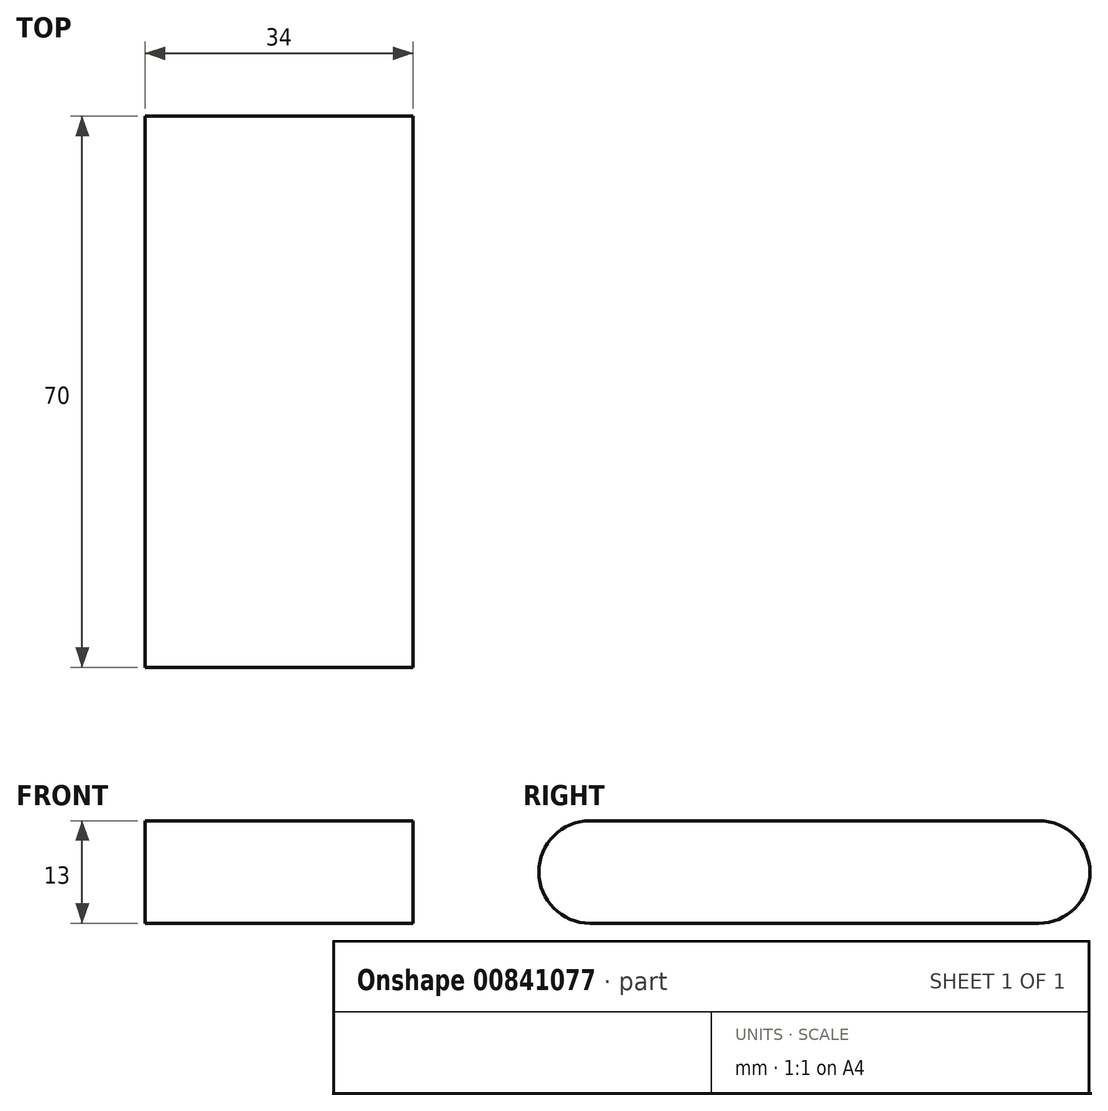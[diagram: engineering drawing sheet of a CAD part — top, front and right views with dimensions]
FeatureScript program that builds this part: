
annotation { "Feature Type Name" : "Feature", "Feature Type Description" : "" }
export const myFeature = defineFeature(function(context is Context, id is Id, definition is map)
    precondition{}
    {
        {
            var Q0;
            Q0=qCreatedBy(makeId("Top.planeOp"),FACE);
            var sketch = newSketch(context, id + "F0", { "sketchPlane" : qUnion([Q0])});
            skLineSegment(sketch, "E0.bottom", {"start": v(0, 0) * mm, "end": v(34, 0) * mm});
            skLineSegment(sketch, "E0.top", {"start": v(0, 70) * mm, "end": v(34, 70) * mm});
            skLineSegment(sketch, "E0.left", {"start": v(0, 0) * mm, "end": v(0, 70) * mm});
            skLineSegment(sketch, "E0.right", {"start": v(34, 0) * mm, "end": v(34, 70) * mm});
            skSolve(sketch);
        }
        {
            var Q0;
            Q0=makeQuery(id+"F0.imprint","IMPRINT",FACE,{"disambiguationData":[TD([[makeQuery(id+"F0.imprint","IMPRINT",EDGE,{"derivedFrom":sQuery(id+"F0.wireOp",EDGE,"E0.bottom")}),1.0]])]});
            extrude(context, id + "F1", {"entities" : qUnion([Q0]), "depth" : 13 * mm, "offsetDistance" : 25 * mm});
        }
        {
            var Q0;
            Q0=makeQuery(id+"F1.opExtrude","CAP_EDGE",EDGE,{"disambiguationData":[OSD([sQuery(id+"F0.wireOp",EDGE,"E0.bottom")])],"isStart":false});
            var Q1;
            Q1=makeQuery(id+"F1.opExtrude","CAP_EDGE",EDGE,{"disambiguationData":[OSD([sQuery(id+"F0.wireOp",EDGE,"E0.bottom")])],"isStart":true});
            fillet(context, id + "F2", {"entities" : qUnion([Q0, Q1]), "radius" : 6.5 * mm, "tangentPropagation" : true, "allowEdgeOverflow" : false});
        }
        {
            var Q0;
            Q0=makeQuery(id+"F1.opExtrude","CAP_EDGE",EDGE,{"disambiguationData":[OSD([sQuery(id+"F0.wireOp",EDGE,"E0.top")])],"isStart":false});
            var Q1;
            Q1=makeQuery(id+"F1.opExtrude","CAP_EDGE",EDGE,{"disambiguationData":[OSD([sQuery(id+"F0.wireOp",EDGE,"E0.top")])],"isStart":true});
            fillet(context, id + "F3", {"entities" : qUnion([Q0, Q1]), "radius" : 6.5 * mm, "tangentPropagation" : true, "allowEdgeOverflow" : false});
        }
    });
